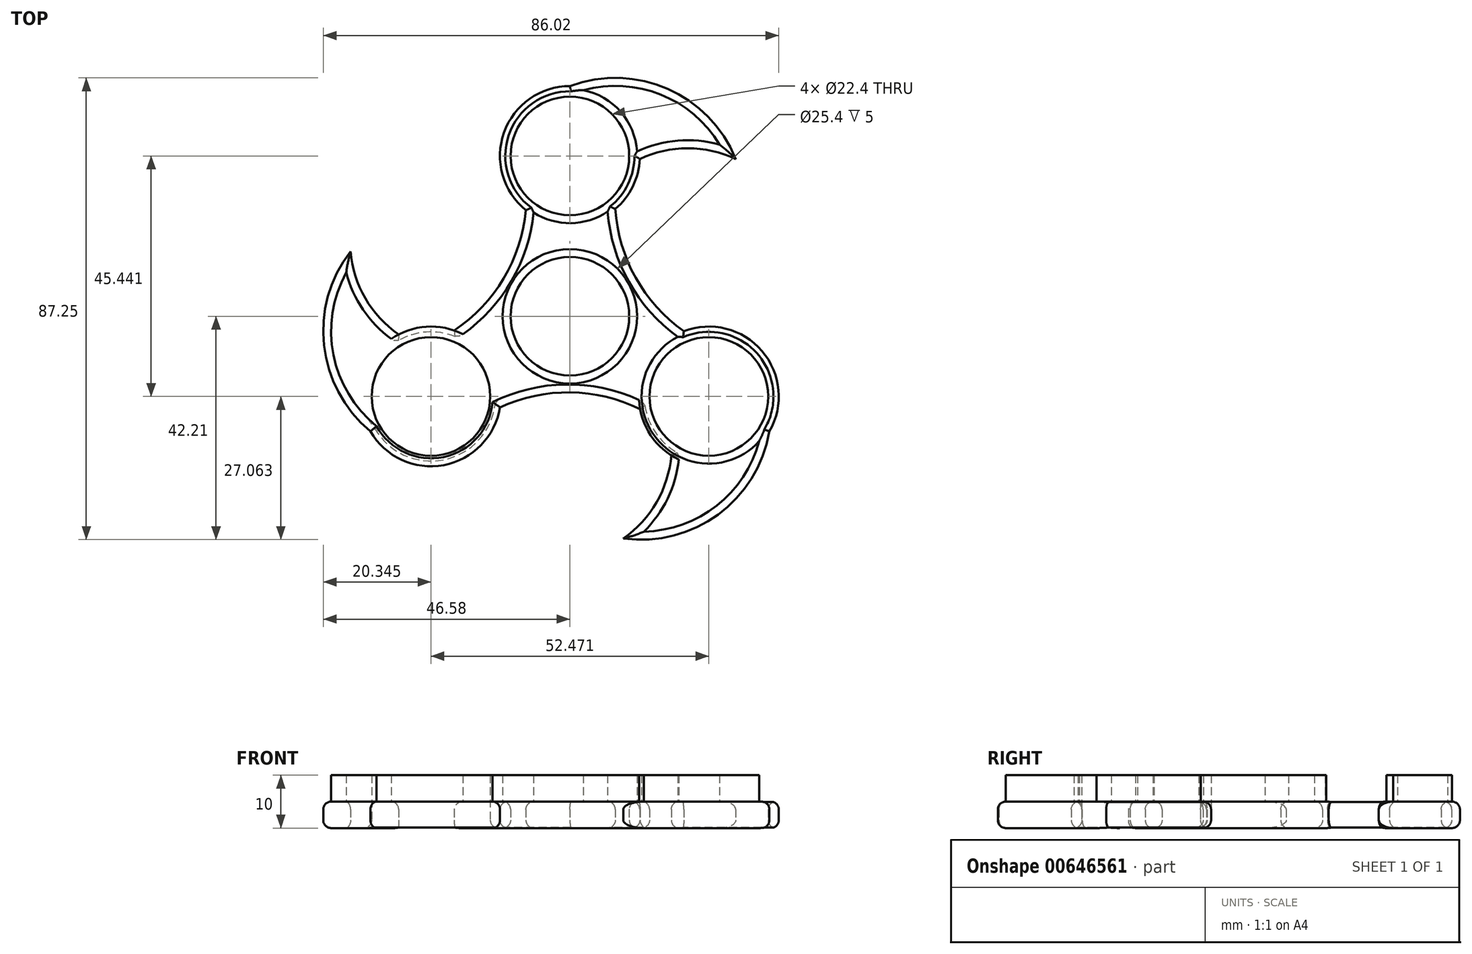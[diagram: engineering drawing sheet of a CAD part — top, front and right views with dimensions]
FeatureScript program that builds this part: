
annotation { "Feature Type Name" : "Feature", "Feature Type Description" : "" }
export const myFeature = defineFeature(function(context is Context, id is Id, definition is map)
    precondition{}
    {
        {
            var Q0;
            Q0=qCreatedBy(makeId("Top.planeOp"),FACE);
            var sketch = newSketch(context, id + "F0", { "sketchPlane" : qUnion([Q0])});
            skCircle(sketch, "E0", {"center": v(0, 0) * mm, "radius": 11.2 * mm});
            skCircle(sketch, "E1", {"center": v(0, 30.3) * mm, "radius": 11.2 * mm});
            skArc(sketch, "E2", {"start": v(8.59, 20.27) * mm, "mid": v(11.87, 24.52) * mm, "end": v(13.19, 29.72) * mm});
            skCircle(sketch, "E3.1.0", {"center": v(-26.24, -15.15) * mm, "radius": 11.2 * mm});
            skArc(sketch, "E3.1.1", {"start": v(-37.67, -21.75) * mm, "mid": v(-23.83, -28.13) * mm, "end": v(-13.2, -17.21) * mm});
            skCircle(sketch, "E3.2.0", {"center": v(26.24, -15.15) * mm, "radius": 11.2 * mm});
            skArc(sketch, "E3.2.1", {"start": v(13.26, -17.57) * mm, "mid": v(15.3, -22.54) * mm, "end": v(19.14, -26.28) * mm});
            skArc(sketch, "E4", {"start": v(31.31, 29.72) * mm, "mid": v(18.45, 42.96) * mm, "end": v(0, 43.5) * mm});
            skArc(sketch, "E5", {"start": v(31.31, 29.72) * mm, "mid": v(22.25, 31.76) * mm, "end": v(13.19, 29.72) * mm});
            skArc(sketch, "E6", {"start": v(8.57, 20.5) * mm, "mid": v(12.37, 7.36) * mm, "end": v(21.5, -2.82) * mm});
            skArc(sketch, "E7.1.0", {"start": v(-41.4, 12.26) * mm, "mid": v(-46.43, -5.5) * mm, "end": v(-37.67, -21.75) * mm});
            skArc(sketch, "E7.1.1", {"start": v(-41.4, 12.26) * mm, "mid": v(-38.63, 3.4) * mm, "end": v(-32.33, -3.44) * mm});
            skArc(sketch, "E7.1.2", {"start": v(-22.05, -2.83) * mm, "mid": v(-12.56, 7.03) * mm, "end": v(-8.3, 20.04) * mm});
            skArc(sketch, "E7.2.0", {"start": v(10.08, -41.98) * mm, "mid": v(27.98, -37.46) * mm, "end": v(37.67, -21.75) * mm});
            skArc(sketch, "E7.2.1", {"start": v(10.08, -41.98) * mm, "mid": v(16.38, -35.15) * mm, "end": v(19.14, -26.28) * mm});
            skArc(sketch, "E7.2.2", {"start": v(13.47, -17.68) * mm, "mid": v(0.2, -14.4) * mm, "end": v(-13.2, -17.21) * mm});
            skArc(sketch, "E8.trimOffspring", {"start": v(0, 43.5) * mm, "mid": v(-12.44, 34.7) * mm, "end": v(-8.3, 20.04) * mm});
            skArc(sketch, "E9.trimOffspring", {"start": v(37.67, -21.75) * mm, "mid": v(36.27, -6.57) * mm, "end": v(21.5, -2.82) * mm});
            skArc(sketch, "E10.trimOffspring", {"start": v(-21.85, -2.7) * mm, "mid": v(-27.17, -1.98) * mm, "end": v(-32.33, -3.44) * mm});
            skSolve(sketch);
        }
        {
            var Q0;
            Q0=makeQuery(id+"F0.imprint","IMPRINT",FACE,{"disambiguationData":[TD([[makeQuery(id+"F0.imprint","IMPRINT",EDGE,{"derivedFrom":sQuery(id+"F0.wireOp",EDGE,"E0")}),-1.0]])]});
            extrude(context, id + "F1", {"entities" : qUnion([Q0]), "depth" : 5 * mm, "offsetDistance" : 25 * mm});
        }
        {
            var Q0;
            Q0=makeQuery(id+"F1.opExtrude","CAP_EDGE",EDGE,{"disambiguationData":[OSD([sQuery(id+"F0.wireOp",EDGE,"E3.1.1")])],"isStart":false});
            var Q1;
            Q1=makeQuery(id+"F1.opExtrude","CAP_EDGE",EDGE,{"disambiguationData":[OSD([sQuery(id+"F0.wireOp",EDGE,"E7.2.2")])],"isStart":false});
            var Q2;
            Q2=makeQuery(id+"F1.opExtrude","CAP_EDGE",EDGE,{"disambiguationData":[OSD([sQuery(id+"F0.wireOp",EDGE,"E7.2.1")])],"isStart":false});
            var Q3;
            Q3=makeQuery(id+"F1.opExtrude","CAP_EDGE",EDGE,{"disambiguationData":[OSD([sQuery(id+"F0.wireOp",EDGE,"E7.2.0")])],"isStart":false});
            var Q4;
            Q4=makeQuery(id+"F1.opExtrude","CAP_EDGE",EDGE,{"disambiguationData":[OSD([sQuery(id+"F0.wireOp",EDGE,"E9.trimOffspring")])],"isStart":false});
            var Q5;
            Q5=makeQuery(id+"F1.opExtrude","CAP_EDGE",EDGE,{"disambiguationData":[OSD([sQuery(id+"F0.wireOp",EDGE,"E3.2.0")])],"isStart":false});
            var Q6;
            Q6=makeQuery(id+"F1.opExtrude","CAP_EDGE",EDGE,{"disambiguationData":[OSD([sQuery(id+"F0.wireOp",EDGE,"E0")])],"isStart":false});
            var Q7;
            Q7=makeQuery(id+"F1.opExtrude","CAP_EDGE",EDGE,{"disambiguationData":[OSD([sQuery(id+"F0.wireOp",EDGE,"E6")])],"isStart":false});
            var Q8;
            Q8=makeQuery(id+"F1.opExtrude","CAP_EDGE",EDGE,{"disambiguationData":[OSD([sQuery(id+"F0.wireOp",EDGE,"E6")])],"isStart":true});
            var Q9;
            Q9=makeQuery(id+"F1.opExtrude","CAP_EDGE",EDGE,{"disambiguationData":[OSD([sQuery(id+"F0.wireOp",EDGE,"E2")])],"isStart":false});
            var Q10;
            Q10=makeQuery(id+"F1.opExtrude","CAP_EDGE",EDGE,{"disambiguationData":[OSD([sQuery(id+"F0.wireOp",EDGE,"E5")])],"isStart":false});
            var Q11;
            Q11=makeQuery(id+"F1.opExtrude","CAP_EDGE",EDGE,{"disambiguationData":[OSD([sQuery(id+"F0.wireOp",EDGE,"E2")])],"isStart":true});
            var Q12;
            Q12=makeQuery(id+"F1.opExtrude","CAP_EDGE",EDGE,{"disambiguationData":[OSD([sQuery(id+"F0.wireOp",EDGE,"E5")])],"isStart":true});
            var Q13;
            Q13=makeQuery(id+"F1.opExtrude","CAP_EDGE",EDGE,{"disambiguationData":[OSD([sQuery(id+"F0.wireOp",EDGE,"E1")])],"isStart":false});
            var Q14;
            Q14=makeQuery(id+"F1.opExtrude","CAP_EDGE",EDGE,{"disambiguationData":[OSD([sQuery(id+"F0.wireOp",EDGE,"E4")])],"isStart":false});
            var Q15;
            Q15=makeQuery(id+"F1.opExtrude","CAP_EDGE",EDGE,{"disambiguationData":[OSD([sQuery(id+"F0.wireOp",EDGE,"E8.trimOffspring")])],"isStart":false});
            var Q16;
            Q16=makeQuery(id+"F1.opExtrude","CAP_EDGE",EDGE,{"disambiguationData":[OSD([sQuery(id+"F0.wireOp",EDGE,"E7.1.2")])],"isStart":false});
            var Q17;
            Q17=makeQuery(id+"F1.opExtrude","CAP_EDGE",EDGE,{"disambiguationData":[OSD([sQuery(id+"F0.wireOp",EDGE,"E7.1.1")])],"isStart":false});
            var Q18;
            Q18=makeQuery(id+"F1.opExtrude","CAP_EDGE",EDGE,{"disambiguationData":[OSD([sQuery(id+"F0.wireOp",EDGE,"E7.1.0")])],"isStart":false});
            var Q19;
            Q19=makeQuery(id+"F1.opExtrude","CAP_FACE",FACE,{"disambiguationData":[OSD([sQuery(id+"F0.wireOp",EDGE,"E0"),sQuery(id+"F0.wireOp",EDGE,"E1"),sQuery(id+"F0.wireOp",EDGE,"E2"),sQuery(id+"F0.wireOp",EDGE,"E3.1.0"),sQuery(id+"F0.wireOp",EDGE,"E3.1.1"),sQuery(id+"F0.wireOp",EDGE,"E3.2.0"),sQuery(id+"F0.wireOp",EDGE,"E3.2.1"),sQuery(id+"F0.wireOp",EDGE,"E4"),sQuery(id+"F0.wireOp",EDGE,"E5"),sQuery(id+"F0.wireOp",EDGE,"E6"),sQuery(id+"F0.wireOp",EDGE,"E7.1.0"),sQuery(id+"F0.wireOp",EDGE,"E7.1.1"),sQuery(id+"F0.wireOp",EDGE,"E7.1.2"),sQuery(id+"F0.wireOp",EDGE,"E7.2.0"),sQuery(id+"F0.wireOp",EDGE,"E7.2.1"),sQuery(id+"F0.wireOp",EDGE,"E7.2.2"),sQuery(id+"F0.wireOp",EDGE,"E8.trimOffspring"),sQuery(id+"F0.wireOp",EDGE,"E9.trimOffspring"),sQuery(id+"F0.wireOp",EDGE,"E10.trimOffspring")])],"isStart":true});
            fillet(context, id + "F2", {"entities" : qUnion([Q0, Q1, Q2, Q3, Q4, Q5, Q6, Q7, Q8, Q9, Q10, Q11, Q12, Q13, Q14, Q15, Q16, Q17, Q18, Q19]), "radius" : 1.5 * mm, "tangentPropagation" : true, "allowEdgeOverflow" : false});
        }
        {
            var Q0;
            Q0=makeQuery(id+"F2.opFillet","SPLIT",FACE,{"disambiguationData":[OD(0.0)],"derivedFrom":makeQuery(id+"F1.opExtrude","CAP_FACE",FACE,{"disambiguationData":[OSD([sQuery(id+"F0.wireOp",EDGE,"E0"),sQuery(id+"F0.wireOp",EDGE,"E1"),sQuery(id+"F0.wireOp",EDGE,"E2"),sQuery(id+"F0.wireOp",EDGE,"E3.1.0"),sQuery(id+"F0.wireOp",EDGE,"E3.1.1"),sQuery(id+"F0.wireOp",EDGE,"E3.2.0"),sQuery(id+"F0.wireOp",EDGE,"E3.2.1"),sQuery(id+"F0.wireOp",EDGE,"E4"),sQuery(id+"F0.wireOp",EDGE,"E5"),sQuery(id+"F0.wireOp",EDGE,"E6"),sQuery(id+"F0.wireOp",EDGE,"E7.1.0"),sQuery(id+"F0.wireOp",EDGE,"E7.1.1"),sQuery(id+"F0.wireOp",EDGE,"E7.1.2"),sQuery(id+"F0.wireOp",EDGE,"E7.2.0"),sQuery(id+"F0.wireOp",EDGE,"E7.2.1"),sQuery(id+"F0.wireOp",EDGE,"E7.2.2"),sQuery(id+"F0.wireOp",EDGE,"E8.trimOffspring"),sQuery(id+"F0.wireOp",EDGE,"E9.trimOffspring"),sQuery(id+"F0.wireOp",EDGE,"E10.trimOffspring")])],"isStart":false})});
            var Q1;
            Q1=makeQuery(id+"F2.opFillet","SPLIT",FACE,{"disambiguationData":[OD(1.0)],"derivedFrom":makeQuery(id+"F1.opExtrude","CAP_FACE",FACE,{"disambiguationData":[OSD([sQuery(id+"F0.wireOp",EDGE,"E0"),sQuery(id+"F0.wireOp",EDGE,"E1"),sQuery(id+"F0.wireOp",EDGE,"E2"),sQuery(id+"F0.wireOp",EDGE,"E3.1.0"),sQuery(id+"F0.wireOp",EDGE,"E3.1.1"),sQuery(id+"F0.wireOp",EDGE,"E3.2.0"),sQuery(id+"F0.wireOp",EDGE,"E3.2.1"),sQuery(id+"F0.wireOp",EDGE,"E4"),sQuery(id+"F0.wireOp",EDGE,"E5"),sQuery(id+"F0.wireOp",EDGE,"E6"),sQuery(id+"F0.wireOp",EDGE,"E7.1.0"),sQuery(id+"F0.wireOp",EDGE,"E7.1.1"),sQuery(id+"F0.wireOp",EDGE,"E7.1.2"),sQuery(id+"F0.wireOp",EDGE,"E7.2.0"),sQuery(id+"F0.wireOp",EDGE,"E7.2.1"),sQuery(id+"F0.wireOp",EDGE,"E7.2.2"),sQuery(id+"F0.wireOp",EDGE,"E8.trimOffspring"),sQuery(id+"F0.wireOp",EDGE,"E9.trimOffspring"),sQuery(id+"F0.wireOp",EDGE,"E10.trimOffspring")])],"isStart":false})});
            extrude(context, id + "F3", {"entities" : qUnion([Q0, Q1]), "operationType" : NewBodyOperationType.ADD, "depth" : 5 * mm, "offsetDistance" : 25 * mm});
        }
    });
